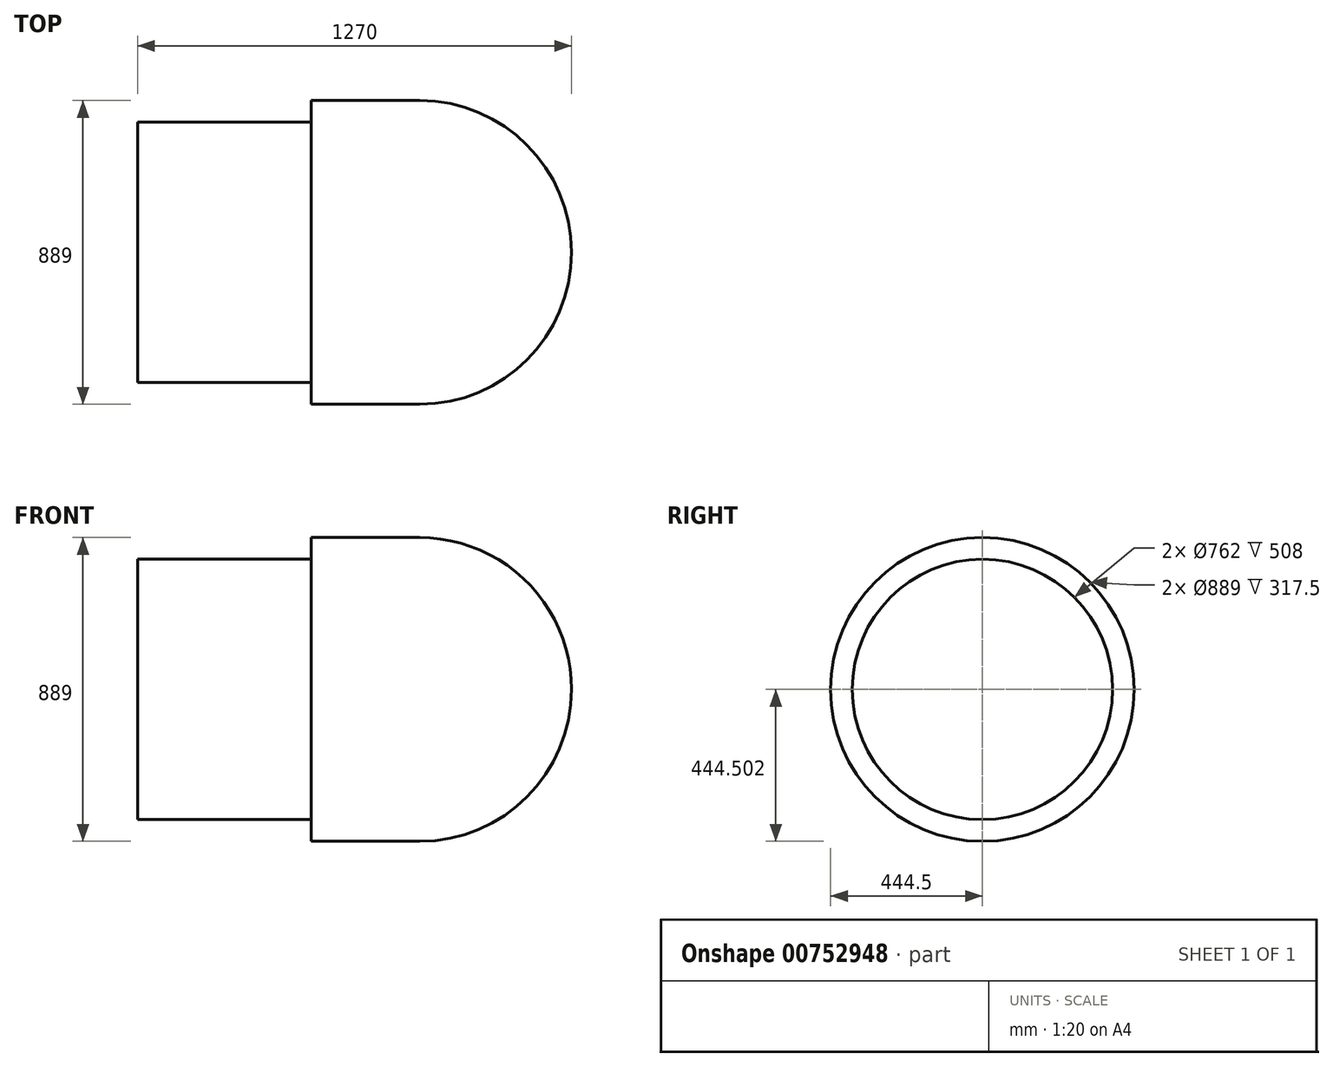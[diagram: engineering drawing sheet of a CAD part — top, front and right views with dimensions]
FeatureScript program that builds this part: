
annotation { "Feature Type Name" : "Feature", "Feature Type Description" : "" }
export const myFeature = defineFeature(function(context is Context, id is Id, definition is map)
    precondition{}
    {
        {
            var Q0;
            Q0=qCreatedBy(makeId("Front.planeOp"),FACE);
            var sketch = newSketch(context, id + "F0", { "sketchPlane" : qUnion([Q0])});
            skLineSegment(sketch, "E0", {"start": v(-1874.26, 0) * mm, "end": v(2213.78, 0) * mm, "construction": true});
            skLineSegment(sketch, "E1.bottom", {"start": v(-637.02, 165.2) * mm, "end": v(-129.02, 165.2) * mm});
            skLineSegment(sketch, "E1.left", {"start": v(-637.02, 165.2) * mm, "end": v(-637.02, -215.8) * mm});
            skLineSegment(sketch, "E2.bottom", {"start": v(-129.02, 228.7) * mm, "end": v(188.48, 228.7) * mm});
            skLineSegment(sketch, "E2.left", {"start": v(-129.02, 228.7) * mm, "end": v(-129.02, 165.2) * mm});
            skArc(sketch, "E3", {"start": v(188.48, 228.7) * mm, "mid": v(502.79, 98.5) * mm, "end": v(632.98, -215.8) * mm});
            skLineSegment(sketch, "E4", {"start": v(865.53, -215.8) * mm, "end": v(-949.64, -215.8) * mm, "construction": true});
            skSolve(sketch);
        }
        {
            var Q0;
            Q0=sQuery(id+"F0.wireOp",EDGE,"E2.bottom");
            var Q1;
            Q1=sQuery(id+"F0.wireOp",EDGE,"E1.left");
            var Q2;
            Q2=sQuery(id+"F0.wireOp",EDGE,"E3");
            var Q3;
            Q3=sQuery(id+"F0.wireOp",EDGE,"E1.bottom");
            var Q4;
            Q4=sQuery(id+"F0.wireOp",EDGE,"E2.left");
            var Q5;
            Q5=sQuery(id+"F0.wireOp",EDGE,"E4");
            revolve(context, id + "F1", {"bodyType" : ToolBodyType.SURFACE, "surfaceOperationType" : NewSurfaceOperationType.NEW, "surfaceEntities" : qUnion([Q0, Q1, Q2, Q3, Q4]), "axis" : qUnion([Q5]), "revolveType" : RevolveType.FULL});
        }
    });
